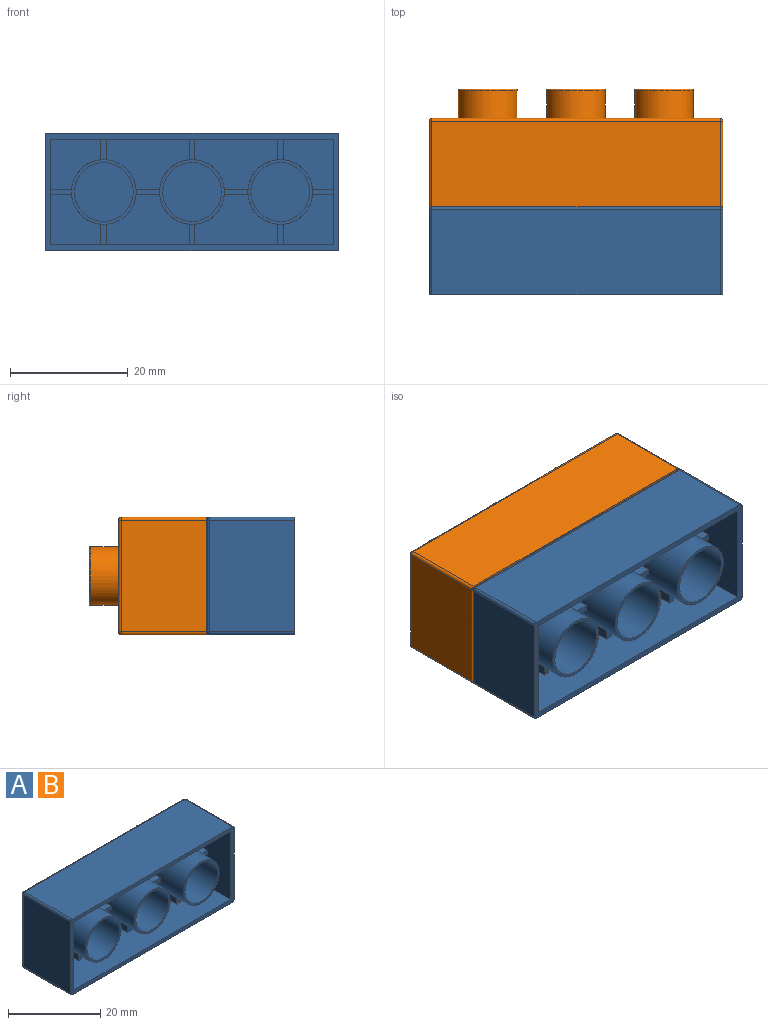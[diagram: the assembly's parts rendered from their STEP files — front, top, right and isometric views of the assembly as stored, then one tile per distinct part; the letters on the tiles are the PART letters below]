
ASSEMBLY  parts=2 mates=1
PART A: 84 faces, bbox 50x20x20 mm
  f0: plane 3.52x1mm, normal (0,-1,0), area 3.5mm2, adj f1,f2,f32,f44
  f1: plane 7x3.52mm, normal (-1,0,0), area 24.7mm2, adj f0,f32,f44,f49
  f2: plane 7x3.52mm, normal (1,0,0), area 24.7mm2, adj f0,f32,f35,f44
  f3: plane 7x3.52mm, normal (0,0,1), area 24.7mm2, adj f5,f30,f39,f41
  f4: plane 7x3.52mm, normal (0,0,-1), area 24.7mm2, adj f5,f30,f38,f41
  f5: plane 3.52x1mm, normal (0,-1,0), area 3.5mm2, adj f3,f4,f30,f41
  f6: plane 7x3.52mm, normal (-1,0,0), area 24.7mm2, adj f8,f37,f44,f53
  f7: plane 7x3.52mm, normal (1,0,0), area 24.7mm2, adj f8,f36,f44,f53
  f8: plane 3.52x1mm, normal (0,-1,0), area 3.5mm2, adj f6,f7,f44,f53
  f9: plane 7x4.05mm, normal (0,0,1), area 28.3mm2, adj f11,f35,f44,f47
  f10: plane 7x4.05mm, normal (0,0,-1), area 28.3mm2, adj f11,f36,f44,f47
  f11: plane 4.05x1mm, normal (0,-1,0), area 4mm2, adj f9,f10,f44,f47
  f12: plane 7x3.52mm, normal (0,0,1), area 24.7mm2, adj f14,f31,f44,f49
  f13: plane 7x3.52mm, normal (0,0,-1), area 24.7mm2, adj f14,f31,f37,f44
  f14: plane 3.52x1mm, normal (0,-1,0), area 3.5mm2, adj f12,f13,f31,f44
  f15: plane 7x3.52mm, normal (1,0,0), area 24.7mm2, adj f17,f32,f39,f41
  f16: plane 7x3.52mm, normal (-1,0,0), area 24.7mm2, adj f17,f32,f34,f41
  f17: plane 3.52x1mm, normal (0,-1,0), area 3.5mm2, adj f15,f16,f32,f41
  f18: plane 7x4.05mm, normal (0,0,1), area 28.3mm2, adj f20,f34,f41,f47
  f19: plane 7x4.05mm, normal (0,0,-1), area 28.3mm2, adj f20,f33,f41,f47
  f20: plane 4.05x1mm, normal (0,-1,0), area 4mm2, adj f18,f19,f41,f47
  f21: plane 7x3.52mm, normal (1,0,0), area 24.7mm2, adj f23,f32,f34,f47
  f22: plane 7x3.52mm, normal (-1,0,0), area 24.7mm2, adj f23,f32,f35,f47
  f23: plane 3.52x1mm, normal (0,-1,0), area 3.5mm2, adj f21,f22,f32,f47
  f24: plane 7x3.52mm, normal (-1,0,0), area 24.7mm2, adj f26,f36,f47,f53
  f25: plane 7x3.52mm, normal (1,0,0), area 24.7mm2, adj f26,f33,f47,f53
  f26: plane 3.52x1mm, normal (0,-1,0), area 3.5mm2, adj f24,f25,f47,f53
  f27: plane 7x3.52mm, normal (1,0,0), area 24.7mm2, adj f29,f38,f41,f53
  f28: plane 7x3.52mm, normal (-1,0,0), area 24.7mm2, adj f29,f33,f41,f53
  f29: plane 3.52x1mm, normal (0,-1,0), area 3.5mm2, adj f27,f28,f41,f53
  f30: plane 18x14mm, normal (-1,0,0), area 245mm2, adj f3,f4,f5,f32,f38,f39,f53,f67
  f31: plane 18x14mm, normal (1,0,0), area 245mm2, adj f12,f13,f14,f32,f37,f49,f53,f67
  f32: plane 48x14mm, normal (0,0,-1), area 651mm2, adj f0,f1,f2,f15,f16,f17,f21,f22
  f33: plane 14x8.5mm, normal (0,-1,0), area 82mm2, adj f19,f25,f28,f41,f47,f53
  f34: plane 14x8.5mm, normal (0,-1,0), area 82mm2, adj f16,f18,f21,f32,f41,f47
  f35: plane 14x8.5mm, normal (0,-1,0), area 82mm2, adj f2,f9,f22,f32,f44,f47
  f36: plane 14x8.5mm, normal (0,-1,0), area 82mm2, adj f7,f10,f24,f44,f47,f53
  f37: plane 8.5x8.5mm, normal (0,-1,0), area 53.7mm2, adj f6,f13,f31,f44,f53
  f38: plane 8.5x8.5mm, normal (0,-1,0), area 53.7mm2, adj f4,f27,f30,f41,f53
  f39: plane 8.5x8.5mm, normal (0,-1,0), area 53.7mm2, adj f3,f15,f30,f32,f41
  f40: cylinder r=5mm len=14mm, axis (0,-1,0), area 439.8mm2, adj f42,f52
  f41: cylinder r=5.5mm len=14mm, axis (0,-1,0), area 455.8mm2, adj f3,f4,f5,f15,f16,f17,f18,f19
  f42: plane 11x11mm, normal (0,-1,0), area 16.5mm2, adj f40,f41
  f43: cylinder r=5mm len=14mm, axis (0,-1,0), area 439.8mm2, adj f45,f51
  f44: cylinder r=5.5mm len=14mm, axis (0,-1,0), area 455.8mm2, adj f0,f1,f2,f6,f7,f8,f9,f10
  f45: plane 11x11mm, normal (0,-1,0), area 16.5mm2, adj f43,f44
  f46: cylinder r=5mm len=14mm, axis (0,-1,0), area 439.8mm2, adj f48,f50
  f47: cylinder r=5.5mm len=14mm, axis (0,-1,0), area 455.8mm2, adj f9,f10,f11,f18,f19,f20,f21,f22
  f48: plane 11x11mm, normal (0,-1,0), area 16.5mm2, adj f46,f47
  f49: plane 8.5x8.5mm, normal (0,-1,0), area 53.7mm2, adj f1,f12,f31,f32,f44
  f50: plane 10x10mm, normal (0,-1,0), area 78.5mm2, adj f46
  f51: plane 10x10mm, normal (0,-1,0), area 78.5mm2, adj f43
  f52: plane 10x10mm, normal (0,-1,0), area 78.5mm2, adj f40
  f53: plane 48x14mm, normal (0,0,1), area 651mm2, adj f6,f7,f8,f24,f25,f26,f27,f28
  f54: sphere r=0.5mm, area 0.4mm2, adj f56,f63,f65
  f55: sphere r=0.5mm, area 0.4mm2, adj f56,f60,f64
  f56: cylinder r=0.5mm len=49mm, axis (1,0,0), area 38.5mm2, adj f54,f55,f66,f69
  f57: sphere r=0.5mm, area 0.4mm2, adj f58,f61,f63
  f58: cylinder r=0.5mm len=14.5mm, axis (0,-1,0), area 11.4mm2, adj f57,f67,f82,f83
  f59: sphere r=0.5mm, area 0.4mm2, adj f60,f61,f62
  f60: cylinder r=0.5mm len=19mm, axis (0,0,1), area 14.9mm2, adj f55,f59,f68,f69
  f61: cylinder r=0.5mm len=49mm, axis (-1,0,0), area 38.5mm2, adj f57,f59,f69,f83
  f62: cylinder r=0.5mm len=14.5mm, axis (0,1,0), area 11.4mm2, adj f59,f67,f68,f83
  f63: cylinder r=0.5mm len=19mm, axis (0,0,-1), area 14.9mm2, adj f54,f57,f69,f82
  f64: cylinder r=0.5mm len=14.5mm, axis (0,1,0), area 11.4mm2, adj f55,f66,f67,f68
  f65: cylinder r=0.5mm len=14.5mm, axis (0,1,0), area 11.4mm2, adj f54,f66,f67,f82
  f66: plane 49x14.5mm, normal (0,0,-1), area 710.5mm2, adj f56,f64,f65,f67
  f67: plane 50x20mm, normal (0,-1,0), area 135.8mm2, adj f30,f31,f32,f53,f58,f62,f64,f65
  f68: plane 19x14.5mm, normal (1,0,0), area 275.5mm2, adj f60,f62,f64,f67
  f69: plane 49x19mm, normal (0,1,0), area 695.4mm2, adj f56,f60,f61,f63,f72,f73,f78
  f70: cylinder r=4.5mm len=9mm, axis (0,-1,0), area 134.3mm2, adj f71,f81
  f71: torus R=4.75mm, axis (0,1,0), area 23.4mm2, adj f70,f72
  f72: cylinder r=5mm len=10mm, axis (0,-1,0), area 149.2mm2, adj f69,f71
  f73: cylinder r=5mm len=10mm, axis (0,-1,0), area 149.2mm2, adj f69,f74
  f74: torus R=4.75mm, axis (0,-1,0), area 23.4mm2, adj f73,f75
  f75: cylinder r=4.5mm len=9mm, axis (0,-1,0), area 134.3mm2, adj f74,f79
  f76: cylinder r=4.5mm len=9mm, axis (0,-1,0), area 134.3mm2, adj f77,f80
  f77: torus R=4.75mm, axis (0,1,0), area 23.4mm2, adj f76,f78
  f78: cylinder r=5mm len=10mm, axis (0,-1,0), area 149.2mm2, adj f69,f77
  f79: plane 9x9mm, normal (0,1,0), area 63.6mm2, adj f75
  f80: plane 9x9mm, normal (0,1,0), area 63.6mm2, adj f76
  f81: plane 9x9mm, normal (0,1,0), area 63.6mm2, adj f70
  f82: plane 19x14.5mm, normal (-1,0,0), area 275.5mm2, adj f58,f63,f65,f67
  f83: plane 49x14.5mm, normal (0,0,1), area 710.5mm2, adj f58,f61,f62,f67
PART B: same geometry as A
PLACE A t=(3.67,9.27,-4.52)mm
PLACE B t=(3.67,24.27,-4.52)mm
MATE slider B.f46 <-> A.f46  axis (0,-1,0) through (-21.33,24.27,-14.52)mm
